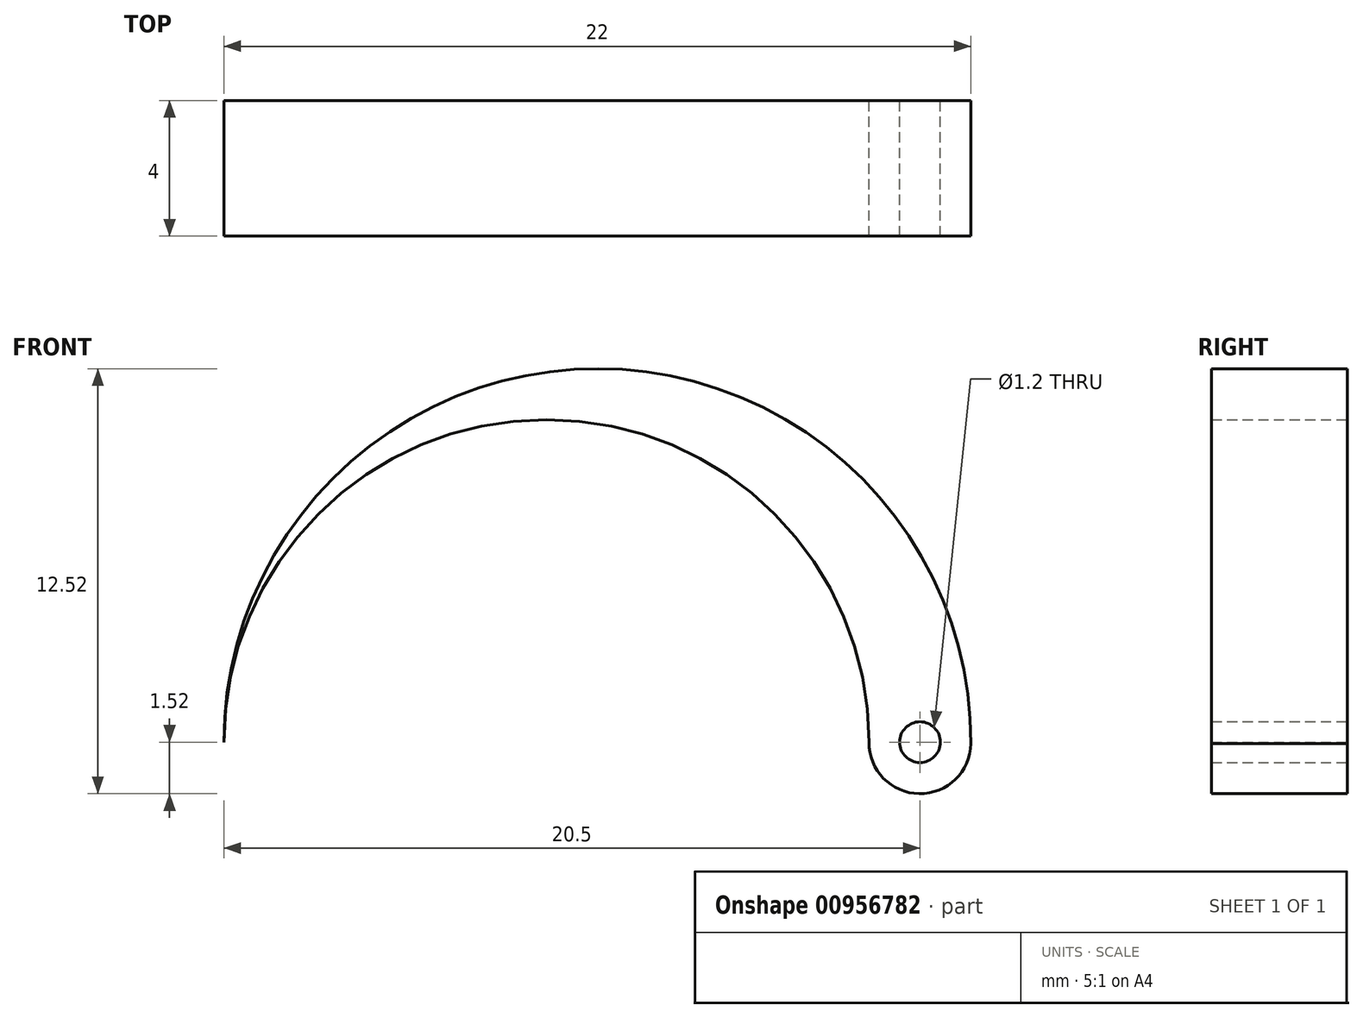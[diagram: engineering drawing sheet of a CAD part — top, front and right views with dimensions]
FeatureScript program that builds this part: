
annotation { "Feature Type Name" : "Feature", "Feature Type Description" : "" }
export const myFeature = defineFeature(function(context is Context, id is Id, definition is map)
    precondition{}
    {
        {
            var Q0;
            Q0=qCreatedBy(makeId("Front.planeOp"),FACE);
            var sketch = newSketch(context, id + "F0", { "sketchPlane" : qUnion([Q0])});
            skLineSegment(sketch, "E0", {"start": v(8, 0) * mm, "end": v(8, 0) * mm});
            skArc(sketch, "E1", {"start": v(11, -0.04) * mm, "mid": v(0.02, 11) * mm, "end": v(-11, 0) * mm});
            skCircle(sketch, "E2", {"center": v(9.5, 0) * mm, "radius": 0.6 * mm});
            skArc(sketch, "E3", {"start": v(8, 0) * mm, "mid": v(9.5, -1.52) * mm, "end": v(11, 0) * mm});
            skArc(sketch, "E4", {"start": v(8, 0) * mm, "mid": v(-1.5, 9.5) * mm, "end": v(-11, 0) * mm});
            skPoint(sketch, "E5.center.orphan", {"position": v(-9.5, 0) * mm});
            skSolve(sketch);
        }
        {
            var Q0;
            {var subQ0=sQuery(id+"F0.wireOp",EDGE,"E1");Q0=makeQuery(id+"F0.imprint","IMPRINT",FACE,{"disambiguationData":[TD([[makeQuery(id+"F0.imprint","IMPRINT",EDGE,{"derivedFrom":subQ0}),1.0]])]});}
            extrude(context, id + "F1", {"entities" : qUnion([Q0]), "depth" : 4 * mm, "offsetDistance" : 25 * mm});
        }
    });
